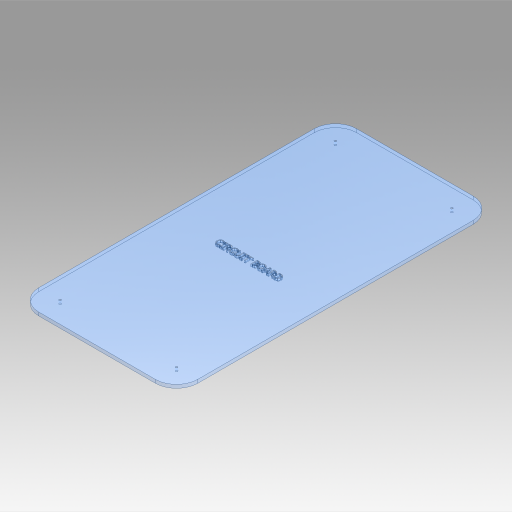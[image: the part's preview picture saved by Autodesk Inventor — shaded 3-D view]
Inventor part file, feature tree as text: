
AUTODESK INVENTOR PART (.ipt)
format: ipt  version: 2023 (Build 270158000, 158)  size: 475,648 bytes
history: native  units: in
note: dims shown in document units (in); Inventor stores cm internally (conversion verified against a paired STEP export)
features: sketch x2, extrude x1, emboss x1
ambient origin geometry x8: Origin, YZ Plane, XZ Plane, XY Plane, X Axis, Y Axis, Z Axis, Center Point
bodies: Solid1 (feature_tree)
feature tree (4):
  extrude  "Extrusion1"  Depth=5.9055in
  emboss  "Emboss1"
  sketch  "Sketch1"  dims[d0=2.9528in d1=5.9055in]
  sketch  "Sketch2"  dims[d2=0.3937in d3=0.3937in d4=0.0394in d5=0.0394in d6=0.0394in d7=0.0394in d8=0.063in d9=0.0in d10=0.0394in d11=0.0in]
